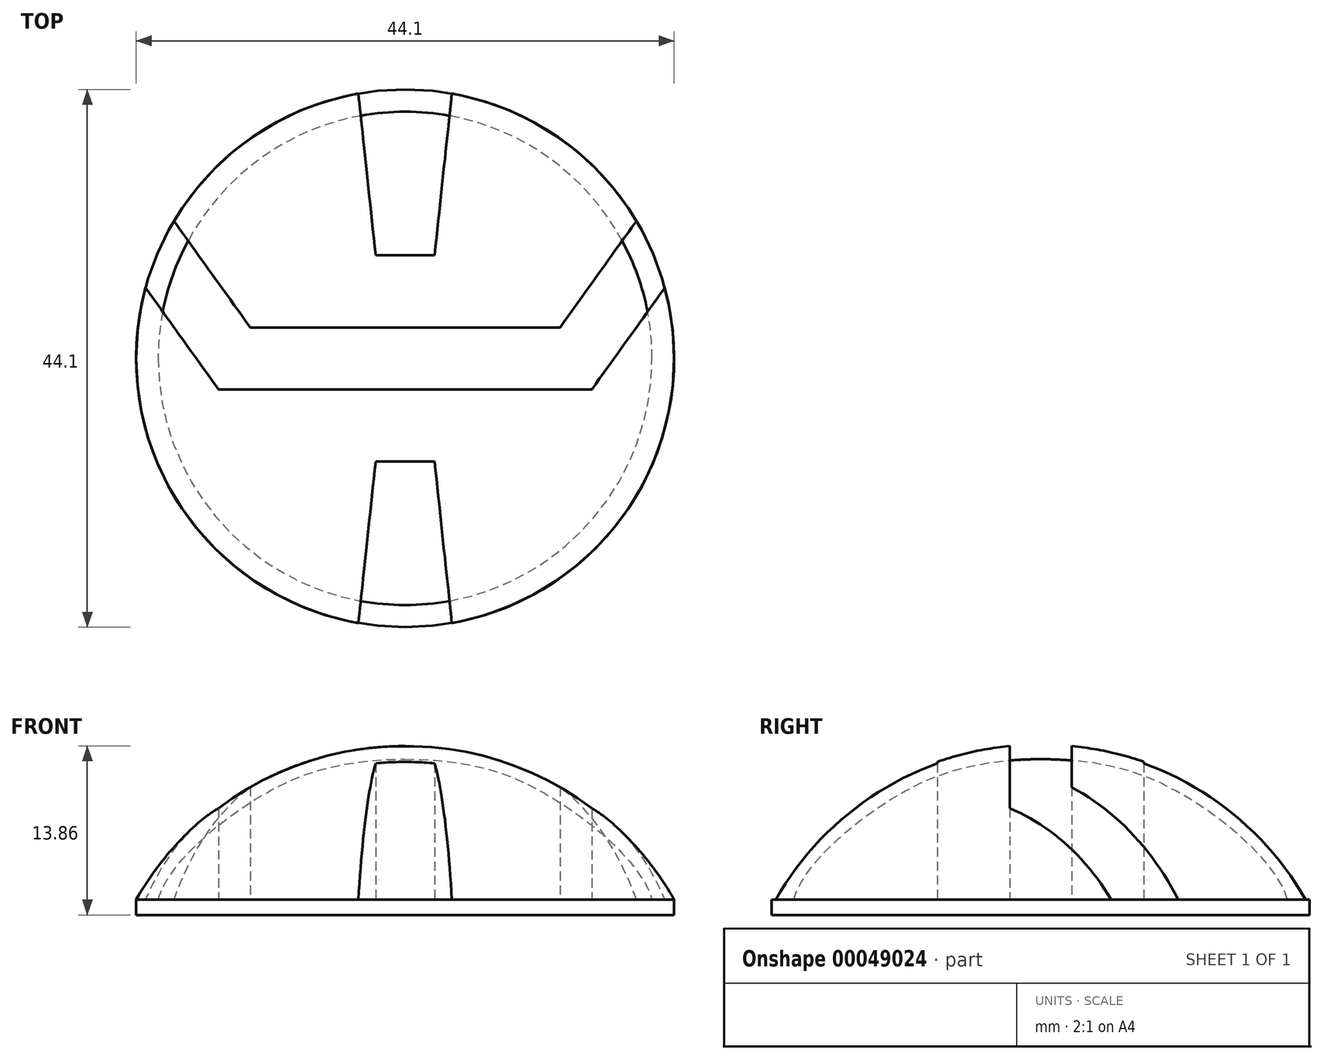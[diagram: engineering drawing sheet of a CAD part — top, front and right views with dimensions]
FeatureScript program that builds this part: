
annotation { "Feature Type Name" : "Feature", "Feature Type Description" : "" }
export const myFeature = defineFeature(function(context is Context, id is Id, definition is map)
    precondition{}
    {
        {
            var Q0;
            Q0=qCreatedBy(makeId("Top.planeOp"),FACE);
            var sketch = newSketch(context, id + "F0", { "sketchPlane" : qUnion([Q0])});
            skCircle(sketch, "E0", {"center": v(0, 0) * mm, "radius": 25.4 * mm});
            skSolve(sketch);
        }
        {
            var Q0;
            Q0 = qSketchRegion(id + "F0", true);
            extrude(context, id + "F1", {"entities" : qUnion([Q0]), "depth" : 12.7 * mm, "hasSecondDirection" : true, "secondDirectionOppositeDirection" : true, "secondDirectionDepth" : 38.1 * mm});
        }
        {
            var Q0;
            Q0=makeQuery(id+"F1.opExtrude","CAP_EDGE",EDGE,{"disambiguationData":[OSD([sQuery(id+"F0.wireOp",EDGE,"E0")])],"isStart":false});
            fillet(context, id + "F2", {"entities" : qUnion([Q0]), "radius" : 25.27 * mm, "allowEdgeOverflow" : false});
        }
        {
            var Q0;
            Q0=qCreatedBy(makeId("Top.planeOp"),FACE);
            var sketch = newSketch(context, id + "F3", { "sketchPlane" : qUnion([Q0])});
            skLineSegment(sketch, "E1", {"start": v(0, 2.54) * mm, "end": v(-12.7, 2.54) * mm});
            skLineSegment(sketch, "E2", {"start": v(-12.7, 2.54) * mm, "end": v(-25.98, 21.06) * mm});
            skLineSegment(sketch, "E3", {"start": v(-25.98, 21.06) * mm, "end": v(-30.11, 18.1) * mm});
            skLineSegment(sketch, "E4", {"start": v(-30.11, 18.1) * mm, "end": v(-15.3, -2.54) * mm});
            skLineSegment(sketch, "E5", {"start": v(-15.3, -2.54) * mm, "end": v(0, -2.54) * mm});
            skLineSegment(sketch, "E6.MirrorCS", {"start": v(0, 2.54) * mm, "end": v(12.7, 2.54) * mm});
            skLineSegment(sketch, "E7.MirrorCS", {"start": v(15.3, -2.54) * mm, "end": v(0, -2.54) * mm});
            skLineSegment(sketch, "E8.MirrorCS", {"start": v(30.11, 18.1) * mm, "end": v(15.3, -2.54) * mm});
            skLineSegment(sketch, "E9.MirrorCS", {"start": v(12.7, 2.54) * mm, "end": v(25.98, 21.06) * mm});
            skLineSegment(sketch, "E10.MirrorCS", {"start": v(25.98, 21.06) * mm, "end": v(30.11, 18.1) * mm});
            skSolve(sketch);
        }
        {
            var Q0;
            Q0=qCreatedBy(makeId("Top.planeOp"),FACE);
            var sketch = newSketch(context, id + "F4", { "sketchPlane" : qUnion([Q0])});
            skLineSegment(sketch, "E11", {"start": v(-4.48, 27.83) * mm, "end": v(-2.42, 8.47) * mm});
            skLineSegment(sketch, "E12", {"start": v(-2.42, 8.47) * mm, "end": v(0, 8.47) * mm});
            skLineSegment(sketch, "E13", {"start": v(-4.48, 27.83) * mm, "end": v(0, 27.83) * mm});
            skLineSegment(sketch, "E14.MirrorCS", {"start": v(4.48, 27.83) * mm, "end": v(0, 27.83) * mm});
            skLineSegment(sketch, "E15.MirrorCS", {"start": v(4.48, 27.83) * mm, "end": v(2.42, 8.47) * mm});
            skLineSegment(sketch, "E16.MirrorCS", {"start": v(2.42, 8.47) * mm, "end": v(0, 8.47) * mm});
            skLineSegment(sketch, "E17.MirrorCS", {"start": v(-2.42, -8.47) * mm, "end": v(0, -8.47) * mm});
            skLineSegment(sketch, "E18.MirrorCS", {"start": v(-4.48, -27.83) * mm, "end": v(-2.42, -8.47) * mm});
            skLineSegment(sketch, "E19.MirrorCS", {"start": v(2.42, -8.47) * mm, "end": v(0, -8.47) * mm});
            skLineSegment(sketch, "E20.MirrorCS", {"start": v(4.48, -27.83) * mm, "end": v(2.42, -8.47) * mm});
            skLineSegment(sketch, "E21.MirrorCS", {"start": v(4.48, -27.83) * mm, "end": v(0, -27.83) * mm});
            skLineSegment(sketch, "E22.MirrorCS", {"start": v(-4.48, -27.83) * mm, "end": v(0, -27.83) * mm});
            skSolve(sketch);
        }
        {
            var Q0;
            Q0=makeQuery(id+"F4.imprint","IMPRINT",FACE,{"disambiguationData":[TD([[makeQuery(id+"F4.imprint","IMPRINT",EDGE,{"derivedFrom":sQuery(id+"F4.wireOp",EDGE,"E11")}),1.0]])]});
            var Q1;
            Q1=makeQuery(id+"F4.imprint","IMPRINT",FACE,{"disambiguationData":[TD([[makeQuery(id+"F4.imprint","IMPRINT",EDGE,{"derivedFrom":sQuery(id+"F4.wireOp",EDGE,"E17.MirrorCS")}),-1.0]])]});
            var Q2;
            Q2=makeQuery(id+"F3.imprint","IMPRINT",FACE,{"disambiguationData":[TD([[makeQuery(id+"F3.imprint","IMPRINT",EDGE,{"derivedFrom":sQuery(id+"F3.wireOp",EDGE,"E1")}),1.0]])]});
            extrude(context, id + "F5", {"entities" : qUnion([Q0, Q1, Q2]), "operationType" : NewBodyOperationType.REMOVE, "depth" : 25.4 * mm, "hasSecondDirection" : true, "secondDirectionOppositeDirection" : true, "secondDirectionDepth" : 25.4 * mm});
        }
        {
            var Q0;
            Q0=qCreatedBy(makeId("Top.planeOp"),FACE);
            var sketch = newSketch(context, id + "F6", { "sketchPlane" : qUnion([Q0])});
            skCircle(sketch, "E23", {"center": v(0, 0) * mm, "radius": 65.62 * mm});
            skSolve(sketch);
        }
        {
            var Q0;
            Q0=makeQuery(id+"F6.imprint","IMPRINT",FACE,{"disambiguationData":[TD([[makeQuery(id+"F6.imprint","IMPRINT",EDGE,{"derivedFrom":sQuery(id+"F6.wireOp",EDGE,"E23")}),1.0]])]});
            extrude(context, id + "F7", {"entities" : qUnion([Q0]), "operationType" : NewBodyOperationType.REMOVE, "oppositeDirection" : true, "depth" : 279.4 * mm});
        }
        {
            var Q0;
            Q0=qCreatedBy(makeId("Front.planeOp"),FACE);
            var sketch = newSketch(context, id + "F8", { "sketchPlane" : qUnion([Q0])});
            skLineSegment(sketch, "E24", {"start": v(0, 0) * mm, "end": v(0, 11.51) * mm});
            skLineSegment(sketch, "E25", {"start": v(0, 0) * mm, "end": v(20.24, 0) * mm});
            skFitSpline(sketch, "E26", {"points": [v(0, 11.51) * mm, v(12.07, 8.34) * mm, v(20.24, 0) * mm], "startDerivative": vector(30.15, -0.3) * mm, "endDerivative": vector(4.7, -17.04) * mm});
            skSolve(sketch);
        }
        {
            var Q0;
            Q0 = qSketchRegion(id + "F8", true);
            var Q1;
            Q1=sQuery(id+"F8.wireOp",EDGE,"E24");
            revolve(context, id + "F9", {"entities" : qUnion([Q0]), "axis" : qUnion([Q1]), "revolveType" : RevolveType.FULL});
        }
        {
            var Q0;
            Q0=makeQuery(id+"F7.boolean.opBoolean","COPY",FACE,{"disambiguationData":[TD([makeQuery(id+"F5.boolean.opBoolean","COPY",FACE,{"derivedFrom":makeQuery(id+"F5.opExtrude","SWEPT_FACE",FACE,{"disambiguationData":[OSD([sQuery(id+"F3.wireOp",EDGE,"E2")])]})})])],"derivedFrom":makeQuery(id+"F7.opExtrude","CAP_FACE",FACE,{"disambiguationData":[OSD([sQuery(id+"F6.wireOp",EDGE,"E23")])],"isStart":true})});
            var sketch = newSketch(context, id + "F10", { "sketchPlane" : qUnion([Q0])});
            skCircle(sketch, "E27", {"center": v(0, 0) * mm, "radius": 22.05 * mm});
            skSolve(sketch);
        }
        {
            var Q0;
            Q0 = qSketchRegion(id + "F10", true);
            extrude(context, id + "F11", {"entities" : qUnion([Q0]), "depth" : 1.27 * mm});
        }
    });
